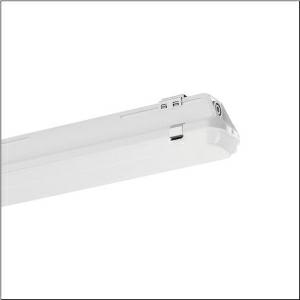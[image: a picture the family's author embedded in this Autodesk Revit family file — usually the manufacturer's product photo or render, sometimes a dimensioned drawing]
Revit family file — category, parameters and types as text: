
# Revit family: monsun_21_51fb20dl440k
name_source: partatom
category: Lighting Fixtures
units: mm (PartAtom-declared; Revit-internal decimal feet)

## family parameters
Cut with Voids When Loaded = No
Host = Face
Light Source = No
Part Type = Normal
Room Calculation Point = No
Round Connector Dimension = Use Diameter
Shared = No

## types (1)
- --- (1 x LED, 4320 lm, 26.6 W, 4000K)
    Apparent Load = 27 VA
    CIE Flux Codes = 45 75 93 94 100
    Color Rendering = 80
    Color Temperature = 4000K
    Default Elevation = 1800 mm
    Description = Monsun 21, damp-proof luminaire, chain hanger, primary optical cover: enclosure, of PC, light emission: direct distribution, primary light characteristic: symmetric, installation type: suspended mounting, surface-mounted, horizontal mounting, vertical mounting, LED, rated luminous flux: 4.320lm, luminous efficacy: 162lm/W, light colour: 840, colour temperature: 4000K, control gear: DALI 2, with terminal, 5-pole, max. 2.5mm², mains connection: 220..240V, AC, 50/60Hz, rated input power: 27W, housing, of glass-fibre reinforced plastic, uncoated, bright grey, incl. chain hanger, length: 1.299mm, width: 90mm, height: 88mm, clip for enclosure, of stainless steel (V2A), ceiling mounting element, of stainless steel (V2A), chain hanger, of stainless steel (V2A), protection rating (complete): IP66, insulation class (complete): insulation class I (protective earthing), certification: CE, ENEC, VDE, UKCA, protection symbol: D, impact resistance: IK08, permissible operating ambient temperature: -25..+35°C, standard: EN 50419, EN 60598-2-1, corresponds to IFS (International Featured Standards) requirements for safety and quality in the food industry, for indoor or canopied outdoor use, no direct snow, no direct sun, no direct rain, LABS conformity tested according to VDMA 24364:2018-05, contact your sales advisor before using the luminaires in applications with unclear chemical exposure, large temperature fluctuations or condensation-forming humidity, packaging unit: 1 piece
    Height = 88 mm
    Lamp = 1 x LED
    Lamp Light Flux = 4320 lm
    Lamp Power = 26.6 W
    Lamp count = 1
    Length = 1299 mm
    Luminous efficacy = 162 lm/W
    Manufacturer = Siteco
    ModVariant = No
    Model = 51FB20DL440K
    Mounting Place = Ceiling
    Mounting Type = Surface mounted
    Number of Poles = 1
    OnlyDefault = Yes
    Power Factor = 1
    Product Name = Monsun 21
    Product group = damp-proof luminaire
    ProductGroupID = 300
    Protection Class = Protection class I
    Protection Degree = IP 66
    RLX_Detail_Level = 1
    RLX_Emergency_Light_Flux = 0 lm
    RLX_Emergency_Type = 0
    RLX_Emergency_Type_DB = No
    RlxData = <blob elided: 93373 chars, md5=a1a4aeef>
    Socket = socket
    Standby Power = 0 W
    System Light Flux = 4320 lm
    System Power = 27 W
    Type Comments = factory setting: luminous flux: 100 % | dim-lin: 254 | 182 mA
    Type Image = l_1319656.jpg
    URL = http://relux.com
    VarID = @adj_037179
    Voltage = 0 V
    Weight = 0.00 kg
    Width = 90 mm

## geometry (parser evidence)
native form markers: Blend x4, Sweep x14
no freeform markers — native parametric forms only
